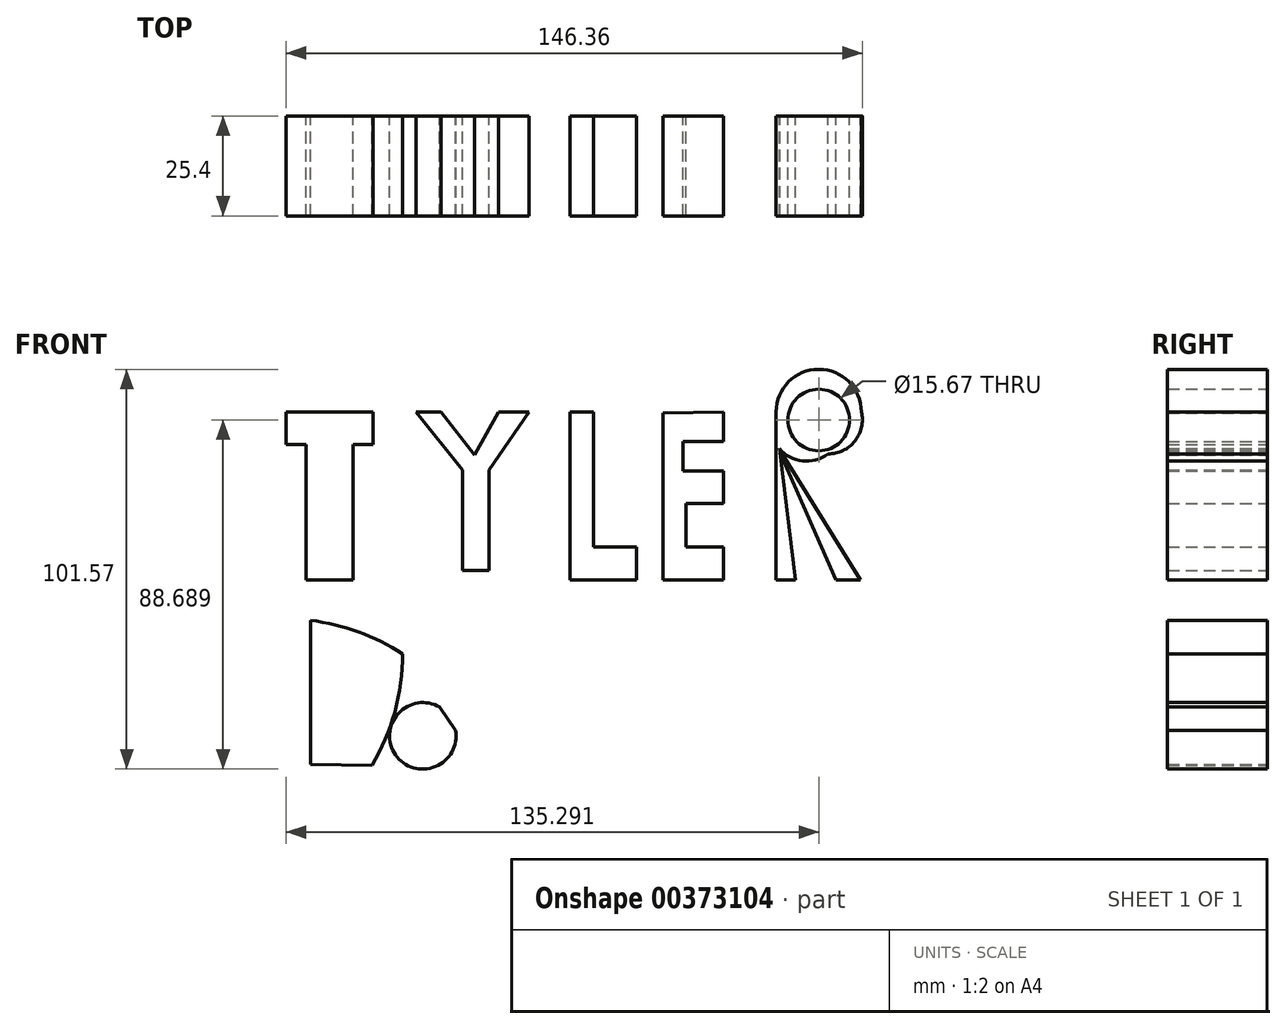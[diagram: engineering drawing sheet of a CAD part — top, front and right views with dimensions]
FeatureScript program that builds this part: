
annotation { "Feature Type Name" : "Feature", "Feature Type Description" : "" }
export const myFeature = defineFeature(function(context is Context, id is Id, definition is map)
    precondition{}
    {
        {
            var Q0;
            Q0=qCreatedBy(makeId("Front.planeOp"),FACE);
            var sketch = newSketch(context, id + "F0", { "sketchPlane" : qUnion([Q0])});
            skLineSegment(sketch, "E0", {"start": v(-81.6, 26.11) * mm, "end": v(-81.55, -8.38) * mm});
            skLineSegment(sketch, "E1", {"start": v(-81.55, -8.38) * mm, "end": v(-93.49, -8.38) * mm});
            skLineSegment(sketch, "E2", {"start": v(-93.49, -8.38) * mm, "end": v(-93.49, 26.1) * mm});
            skLineSegment(sketch, "E3", {"start": v(-93.49, 26.1) * mm, "end": v(-98.59, 26.1) * mm});
            skLineSegment(sketch, "E4", {"start": v(-98.59, 26.1) * mm, "end": v(-98.59, 34.36) * mm});
            skLineSegment(sketch, "E5", {"start": v(-76.48, 26.11) * mm, "end": v(-76.49, 34.36) * mm});
            skLineSegment(sketch, "E6", {"start": v(-98.59, 34.36) * mm, "end": v(-76.49, 34.36) * mm});
            skLineSegment(sketch, "E7", {"start": v(-76.48, 26.11) * mm, "end": v(-81.6, 26.11) * mm});
            skLineSegment(sketch, "E8", {"start": v(-59.24, 34.36) * mm, "end": v(-65.56, 34.36) * mm});
            skLineSegment(sketch, "E9", {"start": v(-59.24, 34.36) * mm, "end": v(-50.73, 23.44) * mm});
            skLineSegment(sketch, "E10", {"start": v(-50.73, 23.44) * mm, "end": v(-44.67, 34.36) * mm});
            skLineSegment(sketch, "E11", {"start": v(-44.67, 34.36) * mm, "end": v(-36.89, 34.36) * mm});
            skLineSegment(sketch, "E12", {"start": v(-44.67, -8.38) * mm, "end": v(-53.85, -8.38) * mm});
            skLineSegment(sketch, "E13", {"start": v(-53.85, -8.38) * mm, "end": v(-53.85, 19.55) * mm});
            skLineSegment(sketch, "E14", {"start": v(-53.85, 19.55) * mm, "end": v(-65.56, 34.36) * mm});
            skLineSegment(sketch, "E15", {"start": v(-47.08, 19.55) * mm, "end": v(-36.89, 34.36) * mm});
            skLineSegment(sketch, "E16", {"start": v(-47.08, 19.55) * mm, "end": v(-47.08, -8.38) * mm});
            skLineSegment(sketch, "E17", {"start": v(-26.44, 34.36) * mm, "end": v(-26.44, -8.38) * mm});
            skLineSegment(sketch, "E18", {"start": v(-26.44, -8.38) * mm, "end": v(-9.6, -8.38) * mm});
            skLineSegment(sketch, "E19", {"start": v(-9.6, -8.38) * mm, "end": v(-9.6, 0) * mm});
            skLineSegment(sketch, "E20", {"start": v(-9.6, 0) * mm, "end": v(-20.56, 0) * mm});
            skLineSegment(sketch, "E21", {"start": v(-20.56, 0) * mm, "end": v(-20.56, 34.36) * mm});
            skLineSegment(sketch, "E22", {"start": v(-20.56, 34.36) * mm, "end": v(-26.44, 34.36) * mm});
            skLineSegment(sketch, "E23", {"start": v(-2.86, 34.36) * mm, "end": v(-2.86, -8.38) * mm});
            skLineSegment(sketch, "E24", {"start": v(-2.86, -8.38) * mm, "end": v(12.52, -8.38) * mm});
            skLineSegment(sketch, "E25", {"start": v(12.52, -8.38) * mm, "end": v(12.52, 0) * mm});
            skLineSegment(sketch, "E26", {"start": v(12.52, 0) * mm, "end": v(3.02, 0) * mm});
            skLineSegment(sketch, "E27", {"start": v(3.02, 0) * mm, "end": v(3.02, 11.06) * mm});
            skLineSegment(sketch, "E28", {"start": v(3.02, 11.06) * mm, "end": v(12.52, 11.06) * mm});
            skLineSegment(sketch, "E29", {"start": v(12.52, 11.06) * mm, "end": v(12.52, 19.32) * mm});
            skLineSegment(sketch, "E30", {"start": v(12.52, 19.32) * mm, "end": v(2.27, 19.32) * mm});
            skLineSegment(sketch, "E31", {"start": v(2.27, 19.32) * mm, "end": v(2.27, 26.85) * mm});
            skLineSegment(sketch, "E32", {"start": v(2.27, 26.85) * mm, "end": v(12.52, 26.85) * mm});
            skLineSegment(sketch, "E33", {"start": v(12.52, 26.85) * mm, "end": v(12.52, 34.36) * mm});
            skLineSegment(sketch, "E34", {"start": v(12.52, 34.36) * mm, "end": v(-2.86, 34.36) * mm});
            skLineSegment(sketch, "E35", {"start": v(25.89, -8.38) * mm, "end": v(25.89, 34.36) * mm});
            skLineSegment(sketch, "E36", {"start": v(25.89, 26.12) * mm, "end": v(47.28, -8.38) * mm});
            skPoint(sketch, "E37.centerSnap0", {"position": v(-87.54, 34.36) * mm});
            skPoint(sketch, "E38.centerSnap0", {"position": v(-54.99, 28.9) * mm});
            skPoint(sketch, "E39.centerSnap0", {"position": v(7.77, 11.06) * mm});
            skArc(sketch, "E40", {"start": v(47.52, 34.36) * mm, "mid": v(36.7, 45.17) * mm, "end": v(25.89, 34.36) * mm});
            skArc(sketch, "E41", {"start": v(39.02, 23.7) * mm, "mid": v(45.9, 26.94) * mm, "end": v(47.52, 34.36) * mm});
            skArc(sketch, "E42", {"start": v(25.89, 26.12) * mm, "mid": v(31.92, 22) * mm, "end": v(39.02, 23.7) * mm});
            skCircle(sketch, "E43", {"center": v(36.7, 32.29) * mm, "radius": 7.83 * mm});
            skLineSegment(sketch, "E44", {"start": v(-92.39, -18.59) * mm, "end": v(-92.39, -55.27) * mm});
            skArc(sketch, "E45", {"start": v(-69.05, -27.09) * mm, "mid": v(-80.26, -21.58) * mm, "end": v(-92.39, -18.59) * mm});
            skArc(sketch, "E46", {"start": v(-76.8, -55.5) * mm, "mid": v(-71, -41.82) * mm, "end": v(-69.05, -27.09) * mm});
            skLineSegment(sketch, "E47", {"start": v(-92.39, -55.27) * mm, "end": v(-76.8, -55.5) * mm});
            skLineSegment(sketch, "E48", {"start": v(-44.25, -55.99) * mm, "end": v(-40.83, -56) * mm});
            skLineSegment(sketch, "E49", {"start": v(-35.5, -46.03) * mm, "end": v(-31.36, -46.03) * mm});
            skLineSegment(sketch, "E50", {"start": v(-85.1, -20.05) * mm, "end": v(-85.11, -8.38) * mm});
            skLineSegment(sketch, "E51", {"start": v(-85.11, -8.38) * mm, "end": v(-53.85, -8.38) * mm});
            skLineSegment(sketch, "E52", {"start": v(-26.44, -8.38) * mm, "end": v(25.89, -8.38) * mm});
            skLineSegment(sketch, "E53", {"start": v(-44.67, -8.38) * mm, "end": v(-26.44, -8.38) * mm});
            skLineSegment(sketch, "E54", {"start": v(47.28, -8.38) * mm, "end": v(41.01, -8.38) * mm});
            skLineSegment(sketch, "E55", {"start": v(41.01, -8.38) * mm, "end": v(25.89, 26.12) * mm});
            skLineSegment(sketch, "E56", {"start": v(30.82, -8.38) * mm, "end": v(25.89, -8.38) * mm});
            skLineSegment(sketch, "E57", {"start": v(30.82, -8.38) * mm, "end": v(25.89, 31.45) * mm});
            skCircle(sketch, "E58", {"center": v(-63.89, -47.96) * mm, "radius": 8.45 * mm});
            skLineSegment(sketch, "E59", {"start": v(-71, -41.82) * mm, "end": v(-69.7, -41.82) * mm});
            skLineSegment(sketch, "E60", {"start": v(-69.7, -41.82) * mm, "end": v(-72.82, -47.96) * mm});
            skLineSegment(sketch, "E61", {"start": v(-72.82, -47.96) * mm, "end": v(-71, -44.38) * mm});
            skLineSegment(sketch, "E62", {"start": v(-81.55, -5.95) * mm, "end": v(-53.85, -5.92) * mm});
            skLineSegment(sketch, "E63", {"start": v(-53.85, -5.92) * mm, "end": v(-26.44, -5.88) * mm});
            skLineSegment(sketch, "E64", {"start": v(-26.44, -5.88) * mm, "end": v(-2.86, -5.85) * mm});
            skLineSegment(sketch, "E65", {"start": v(25.89, -5.82) * mm, "end": v(-55.56, -46.53) * mm});
            skLineSegment(sketch, "E66", {"start": v(-55.56, -46.53) * mm, "end": v(-69.05, -27.09) * mm});
            skLineSegment(sketch, "E67", {"start": v(11.9, -12.8) * mm, "end": v(47.28, -8.38) * mm});
            skLineSegment(sketch, "E68", {"start": v(-92.39, -18.59) * mm, "end": v(-93.49, -8.38) * mm});
            skLineSegment(sketch, "E69", {"start": v(-76.49, 34.36) * mm, "end": v(-65.56, 34.36) * mm});
            skLineSegment(sketch, "E70", {"start": v(-36.89, 34.36) * mm, "end": v(-26.44, 34.36) * mm});
            skLineSegment(sketch, "E71", {"start": v(-19.7, 33.87) * mm, "end": v(12.52, 34.36) * mm});
            skLineSegment(sketch, "E72", {"start": v(-76.8, -55.5) * mm, "end": v(-64.49, -56.38) * mm});
            skLineSegment(sketch, "E73", {"start": v(14.3, 34.36) * mm, "end": v(12.52, 34.36) * mm});
            skSolve(sketch);
        }
        {
            var Q0;
            {var subQ5=sQuery(id+"F0.wireOp",EDGE,"E3");Q0=makeQuery(id+"F0.imprint","IMPRINT",FACE,{"disambiguationData":[TD([[makeQuery(id+"F0.imprint","IMPRINT",EDGE,{"derivedFrom":subQ5}),-1.0]])]});}
            var Q1;
            {var subQ1=sQuery(id+"F0.wireOp",EDGE,"E1");Q1=makeQuery(id+"F0.imprint","IMPRINT",FACE,{"disambiguationData":[TD([[makeQuery(id+"F0.imprint","IMPRINT",EDGE,{"derivedFrom":subQ1}),-1.0]])]});}
            var Q2;
            {var subQ5=sQuery(id+"F0.wireOp",EDGE,"E8");Q2=makeQuery(id+"F0.imprint","IMPRINT",FACE,{"disambiguationData":[TD([[makeQuery(id+"F0.imprint","IMPRINT",EDGE,{"derivedFrom":subQ5}),1.0]])]});}
            var Q3;
            {var subQ0=sQuery(id+"F0.wireOp",EDGE,"E10");var subQ1=sQuery(id+"F0.wireOp",EDGE,"E9");var subQ2=makeQuery(id+"F0.imprint","INTERSECT",VERTEX,{"derivedFrom":[subQ1,subQ0]});Q3=makeQuery(id+"F0.imprint","IMPRINT",FACE,{"disambiguationData":[TD([[makeQuery(id+"F0.imprint","IMPRINT",EDGE,{"disambiguationData":[TD([[subQ2,1.0]])],"derivedFrom":subQ1}),1.0]])]});}
            var Q4;
            {var subQ6=sQuery(id+"F0.wireOp",EDGE,"E17");Q4=makeQuery(id+"F0.imprint","IMPRINT",FACE,{"disambiguationData":[TD([[makeQuery(id+"F0.imprint","IMPRINT",EDGE,{"derivedFrom":subQ6}),1.0]])]});}
            var Q5;
            {var subQ0=sQuery(id+"F0.wireOp",EDGE,"E19");Q5=makeQuery(id+"F0.imprint","IMPRINT",FACE,{"disambiguationData":[TD([[makeQuery(id+"F0.imprint","IMPRINT",EDGE,{"derivedFrom":subQ0}),1.0]])]});}
            var Q6;
            {var subQ0=sQuery(id+"F0.wireOp",EDGE,"E21");var subQ1=sQuery(id+"F0.wireOp",EDGE,"E20");var subQ2=makeQuery(id+"F0.imprint","INTERSECT",VERTEX,{"derivedFrom":[subQ1,subQ0]});Q6=makeQuery(id+"F0.imprint","IMPRINT",FACE,{"disambiguationData":[TD([[makeQuery(id+"F0.imprint","IMPRINT",EDGE,{"disambiguationData":[TD([[subQ2,1.0]])],"derivedFrom":subQ1}),-1.0]])]});}
            var Q7;
            {var subQ7=sQuery(id+"F0.wireOp",EDGE,"E23");Q7=makeQuery(id+"F0.imprint","IMPRINT",FACE,{"disambiguationData":[TD([[makeQuery(id+"F0.imprint","IMPRINT",EDGE,{"derivedFrom":subQ7}),1.0]])]});}
            var Q8;
            {var subQ0=sQuery(id+"F0.wireOp",EDGE,"E39");var subQ1=sQuery(id+"F0.wireOp",EDGE,"E28");var subQ2=makeQuery(id+"F0.imprint","INTERSECT",VERTEX,{"disambiguationData":[OD(0.0)],"derivedFrom":[subQ1,subQ0]});Q8=makeQuery(id+"F0.imprint","IMPRINT",FACE,{"disambiguationData":[TD([[makeQuery(id+"F0.imprint","IMPRINT",EDGE,{"disambiguationData":[TD([[subQ2,-1.0]])],"derivedFrom":subQ1}),-1.0]])]});}
            var Q9;
            {var subQ0=sQuery(id+"F0.wireOp",EDGE,"E29");var subQ1=sQuery(id+"F0.wireOp",EDGE,"E28");var subQ2=makeQuery(id+"F0.imprint","INTERSECT",VERTEX,{"derivedFrom":[subQ1,subQ0]});Q9=makeQuery(id+"F0.imprint","IMPRINT",FACE,{"disambiguationData":[TD([[makeQuery(id+"F0.imprint","IMPRINT",EDGE,{"disambiguationData":[TD([[subQ2,1.0]])],"derivedFrom":subQ1}),1.0]])]});}
            var Q10;
            {var subQ0=sQuery(id+"F0.wireOp",EDGE,"E30");var subQ1=sQuery(id+"F0.wireOp",EDGE,"E29");var subQ2=makeQuery(id+"F0.imprint","INTERSECT",VERTEX,{"derivedFrom":[subQ1,subQ0]});Q10=makeQuery(id+"F0.imprint","IMPRINT",FACE,{"disambiguationData":[TD([[makeQuery(id+"F0.imprint","IMPRINT",EDGE,{"disambiguationData":[TD([[subQ2,1.0]])],"derivedFrom":subQ1}),1.0]])]});}
            var Q11;
            {var subQ0=sQuery(id+"F0.wireOp",EDGE,"E39");var subQ1=sQuery(id+"F0.wireOp",EDGE,"E30");var subQ2=makeQuery(id+"F0.imprint","INTERSECT",VERTEX,{"disambiguationData":[OD(0.0)],"derivedFrom":[subQ1,subQ0]});Q11=makeQuery(id+"F0.imprint","IMPRINT",FACE,{"disambiguationData":[TD([[makeQuery(id+"F0.imprint","IMPRINT",EDGE,{"disambiguationData":[TD([[subQ2,-1.0]])],"derivedFrom":subQ1}),-1.0]])]});}
            var Q12;
            {var subQ0=sQuery(id+"F0.wireOp",EDGE,"E56");Q12=makeQuery(id+"F0.imprint","IMPRINT",FACE,{"disambiguationData":[TD([[makeQuery(id+"F0.imprint","IMPRINT",EDGE,{"derivedFrom":subQ0}),-1.0]])]});}
            var Q13;
            {var subQ0=sQuery(id+"F0.wireOp",EDGE,"E54");Q13=makeQuery(id+"F0.imprint","IMPRINT",FACE,{"disambiguationData":[TD([[makeQuery(id+"F0.imprint","IMPRINT",EDGE,{"derivedFrom":subQ0}),-1.0]])]});}
            var Q14;
            {var subQ0=sQuery(id+"F0.wireOp",EDGE,"E52");var subQ1=sQuery(id+"F0.wireOp",EDGE,"6maoY9H0-xNBk-pj6t-KRey-hQ20uvlxjACd");var subQ2=makeQuery(id+"F0.imprint","INTERSECT",VERTEX,{"disambiguationData":[OD(0.0)],"derivedFrom":[subQ1,subQ0]});Q14=makeQuery(id+"F0.imprint","IMPRINT",FACE,{"disambiguationData":[TD([[makeQuery(id+"F0.imprint","IMPRINT",EDGE,{"disambiguationData":[TD([[subQ2,-1.0]])],"derivedFrom":subQ1}),1.0]])]});}
            var Q15;
            {var subQ4=sQuery(id+"F0.wireOp",EDGE,"E44");Q15=makeQuery(id+"F0.imprint","IMPRINT",FACE,{"disambiguationData":[TD([[makeQuery(id+"F0.imprint","IMPRINT",EDGE,{"derivedFrom":subQ4}),1.0]])]});}
            var Q16;
            {var subQ0=sQuery(id+"F0.wireOp",EDGE,"E60");Q16=makeQuery(id+"F0.imprint","IMPRINT",FACE,{"disambiguationData":[TD([[makeQuery(id+"F0.imprint","IMPRINT",EDGE,{"derivedFrom":subQ0}),-1.0]])]});}
            var Q17;
            {var subQ0=sQuery(id+"F0.wireOp",EDGE,"E10");var subQ1=sQuery(id+"F0.wireOp",EDGE,"E9");var subQ2=makeQuery(id+"F0.imprint","INTERSECT",VERTEX,{"derivedFrom":[subQ1,subQ0]});Q17=makeQuery(id+"F0.imprint","IMPRINT",FACE,{"disambiguationData":[TD([[makeQuery(id+"F0.imprint","IMPRINT",EDGE,{"disambiguationData":[TD([[subQ2,1.0]])],"derivedFrom":subQ1}),-1.0]])]});}
            var Q18;
            {var subQ1=sQuery(id+"F0.wireOp",EDGE,"E35");var subQ3=sQuery(id+"F0.wireOp",EDGE,"E57");var subQ4=makeQuery(id+"F0.imprint","INTERSECT",VERTEX,{"derivedFrom":[subQ1,subQ3]});Q18=makeQuery(id+"F0.imprint","IMPRINT",FACE,{"disambiguationData":[TD([[makeQuery(id+"F0.imprint","IMPRINT",EDGE,{"disambiguationData":[TD([[subQ4,1.0]])],"derivedFrom":subQ3}),1.0]])]});}
            var Q19;
            {var subQ1=sQuery(id+"F0.wireOp",EDGE,"E40");Q19=makeQuery(id+"F0.imprint","IMPRINT",FACE,{"disambiguationData":[TD([[makeQuery(id+"F0.imprint","IMPRINT",EDGE,{"derivedFrom":subQ1}),1.0]])]});}
            var Q20;
            {var subQ1=sQuery(id+"F0.wireOp",EDGE,"E36");var subQ3=sQuery(id+"F0.wireOp",EDGE,"E57");var subQ4=makeQuery(id+"F0.imprint","INTERSECT",VERTEX,{"derivedFrom":[subQ1,subQ3]});Q20=makeQuery(id+"F0.imprint","IMPRINT",FACE,{"disambiguationData":[TD([[makeQuery(id+"F0.imprint","IMPRINT",EDGE,{"disambiguationData":[TD([[subQ4,-1.0]])],"derivedFrom":subQ3}),1.0]])]});}
            var Q21;
            {var subQ0=sQuery(id+"F0.wireOp",EDGE,"E37");var subQ1=sQuery(id+"F0.wireOp",EDGE,"E0");var subQ2=makeQuery(id+"F0.imprint","INTERSECT",VERTEX,{"disambiguationData":[OD(0.0)],"derivedFrom":[subQ1,subQ0]});Q21=makeQuery(id+"F0.imprint","IMPRINT",FACE,{"disambiguationData":[TD([[makeQuery(id+"F0.imprint","IMPRINT",EDGE,{"disambiguationData":[TD([[subQ2,1.0]])],"derivedFrom":subQ0}),1.0]])]});}
            var Q22;
            {var subQ1=sQuery(id+"F0.wireOp",EDGE,"E36");var subQ3=sQuery(id+"F0.wireOp",EDGE,"E57");var subQ4=makeQuery(id+"F0.imprint","INTERSECT",VERTEX,{"derivedFrom":[subQ1,subQ3]});Q22=makeQuery(id+"F0.imprint","IMPRINT",FACE,{"disambiguationData":[TD([[makeQuery(id+"F0.imprint","IMPRINT",EDGE,{"disambiguationData":[TD([[subQ4,1.0]])],"derivedFrom":subQ3}),1.0]])]});}
            var Q23;
            {var subQ1=sQuery(id+"F0.wireOp",EDGE,"E20");var subQ5=sQuery(id+"F0.wireOp",EDGE,"E21");var subQ6=makeQuery(id+"F0.imprint","INTERSECT",VERTEX,{"derivedFrom":[subQ1,subQ5]});Q23=makeQuery(id+"F0.imprint","IMPRINT",FACE,{"disambiguationData":[TD([[makeQuery(id+"F0.imprint","IMPRINT",EDGE,{"disambiguationData":[TD([[subQ6,1.0]])],"derivedFrom":subQ1}),1.0]])]});}
            var Q24;
            {var subQ0=sQuery(id+"F0.wireOp",EDGE,"E39");var subQ1=sQuery(id+"F0.wireOp",EDGE,"E28");var subQ2=makeQuery(id+"F0.imprint","INTERSECT",VERTEX,{"disambiguationData":[OD(0.0)],"derivedFrom":[subQ1,subQ0]});Q24=makeQuery(id+"F0.imprint","IMPRINT",FACE,{"disambiguationData":[TD([[makeQuery(id+"F0.imprint","IMPRINT",EDGE,{"disambiguationData":[TD([[subQ2,-1.0]])],"derivedFrom":subQ1}),1.0]])]});}
            extrude(context, id + "F1", {"entities" : qUnion([Q0, Q1, Q2, Q3, Q4, Q5, Q6, Q7, Q8, Q9, Q10, Q11, Q12, Q13, Q14, Q15, Q16, Q17, Q18, Q19, Q20, Q21, Q22, Q23, Q24]), "depth" : 25.4 * mm});
        }
        {
            var Q0;
            {var subQ0=sQuery(id+"F0.wireOp",EDGE,"E60");Q0=makeQuery(id+"F0.imprint","IMPRINT",FACE,{"disambiguationData":[TD([[makeQuery(id+"F0.imprint","IMPRINT",EDGE,{"derivedFrom":subQ0}),1.0]])]});}
            extrude(context, id + "F2", {"entities" : qUnion([Q0]), "operationType" : NewBodyOperationType.ADD, "depth" : 25.4 * mm});
        }
    });
